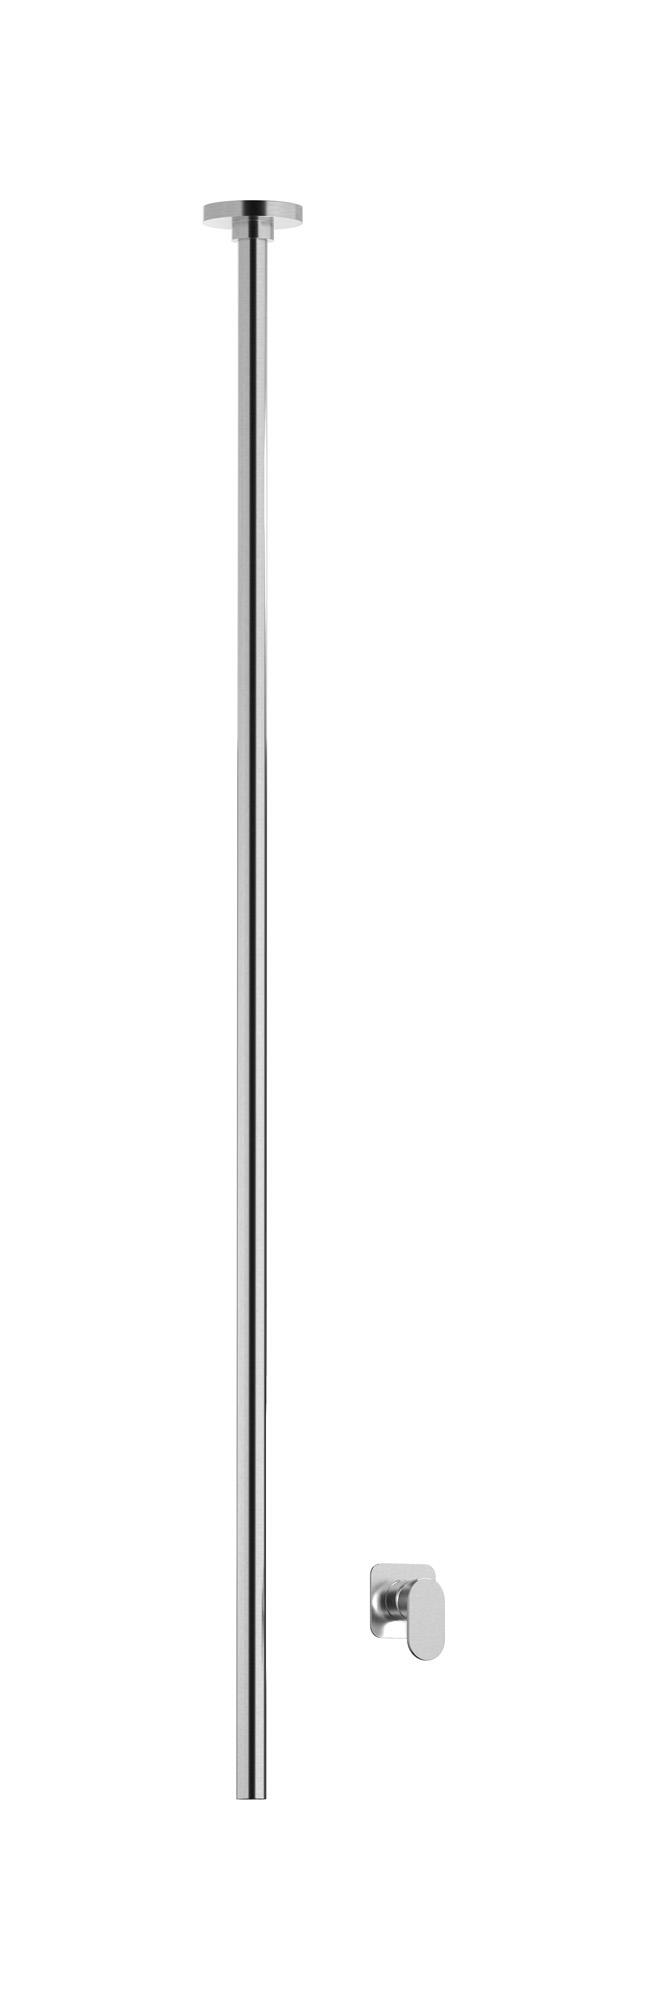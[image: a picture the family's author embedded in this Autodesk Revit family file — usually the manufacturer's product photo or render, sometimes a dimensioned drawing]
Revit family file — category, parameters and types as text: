
# Revit family: SB210
name_source: partatom
category: Apparecchi idraulici
units: mm (PartAtom-declared; Revit-internal decimal feet)

## family parameters
Basato su piano di lavoro = No
Condiviso = No
Mantieni orientamento annotazione = No
Numero OmniClass = 23.45.55.17
Punto di calcolo locali = No
Quota connettore circolare = Usa diametro
Sempre verticale = Sì
Taglio con vuoti quando caricato = No
Tipo di parte = Normale
Titolo OmniClass = Mixing Faucets

## types (4) — shared parameters
Cold water inlet = 10 mm  [stored 0.0328084 ft]
Commenti sul tipo = Mixer
Connessione CW = No
Connessione HW = No
Connessione di scarico = No
Connessione di ventilazione = No
Descrizione = Ceiling spout with wall mounted mixer
Hot water inlet = 10 mm  [stored 0.0328084 ft]
Produttore = IB Rubinetterie S.p.A.
URL = https://www.weareib.it
zero-valued in all types: Prospetto di default

## per-type parameters (varying)
| type | Finishes surface | Immagine tipo | Modello |
| Chrome | IB_Chrome | SB210CC.jpg | SB210CC |
| Brushed nickel | IB_Brushed nickel | SB210SS.jpg | SB210SS |
| Matt black | IB_matt black | SB210NP.jpg | SB210NP |
| Rose gold | IB_Rose gold | SB210RS.jpg | SB210RS |

note: [stored X ft] marks values corroborated as IEEE doubles in the binary element streams (Revit-internal decimal feet)
